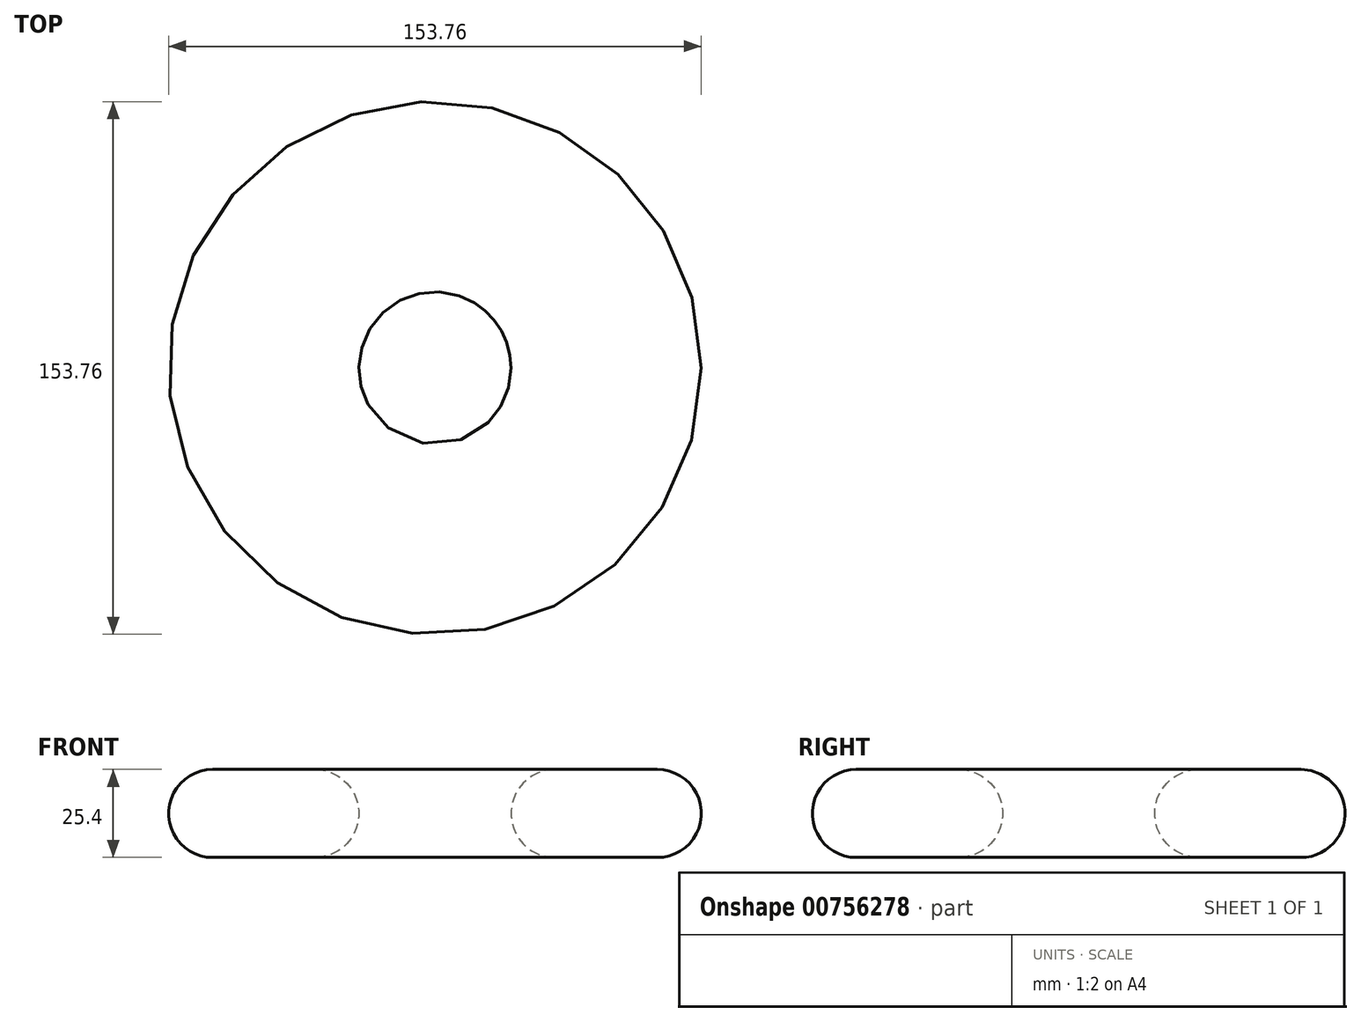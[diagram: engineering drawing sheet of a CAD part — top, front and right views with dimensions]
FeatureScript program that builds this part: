
annotation { "Feature Type Name" : "Feature", "Feature Type Description" : "" }
export const myFeature = defineFeature(function(context is Context, id is Id, definition is map)
    precondition{}
    {
        {
            var Q0;
            Q0=qCreatedBy(makeId("Top.planeOp"),FACE);
            var sketch = newSketch(context, id + "F0", { "sketchPlane" : qUnion([Q0])});
            skCircle(sketch, "E0", {"center": v(0, 0) * mm, "radius": 76.88 * mm});
            skCircle(sketch, "E1", {"center": v(0, 0) * mm, "radius": 21.95 * mm});
            skSolve(sketch);
        }
        {
            var Q0;
            Q0=makeQuery(id+"F0.imprint","IMPRINT",FACE,{"disambiguationData":[TD([[makeQuery(id+"F0.imprint","IMPRINT",EDGE,{"derivedFrom":sQuery(id+"F0.wireOp",EDGE,"E0")}),1.0]])]});
            extrude(context, id + "F1", {"entities" : qUnion([Q0]), "depth" : 25.4 * mm, "offsetDistance" : 25.4 * mm});
        }
        {
            var Q0;
            Q0=makeQuery(id+"F1.opExtrude","CAP_EDGE",EDGE,{"disambiguationData":[OSD([sQuery(id+"F0.wireOp",EDGE,"E0")])],"isStart":false});
            fillet(context, id + "F2", {"entities" : qUnion([Q0]), "radius" : 12.7 * mm, "tangentPropagation" : true, "allowEdgeOverflow" : false});
        }
        {
            var Q0;
            Q0=makeQuery(id+"F1.opExtrude","CAP_EDGE",EDGE,{"disambiguationData":[OSD([sQuery(id+"F0.wireOp",EDGE,"E0")])],"isStart":true});
            fillet(context, id + "F3", {"entities" : qUnion([Q0]), "radius" : 12.7 * mm, "tangentPropagation" : true, "allowEdgeOverflow" : false});
        }
        {
            var Q0;
            Q0=makeQuery(id+"F1.opExtrude","CAP_EDGE",EDGE,{"disambiguationData":[OSD([sQuery(id+"F0.wireOp",EDGE,"E1")])],"isStart":false});
            fillet(context, id + "F4", {"entities" : qUnion([Q0]), "radius" : 12.7 * mm, "tangentPropagation" : true, "allowEdgeOverflow" : false});
        }
        {
            var Q0;
            Q0=makeQuery(id+"F1.opExtrude","CAP_EDGE",EDGE,{"disambiguationData":[OSD([sQuery(id+"F0.wireOp",EDGE,"E1")])],"isStart":true});
            fillet(context, id + "F5", {"entities" : qUnion([Q0]), "radius" : 12.7 * mm, "tangentPropagation" : true, "allowEdgeOverflow" : false});
        }
    });
